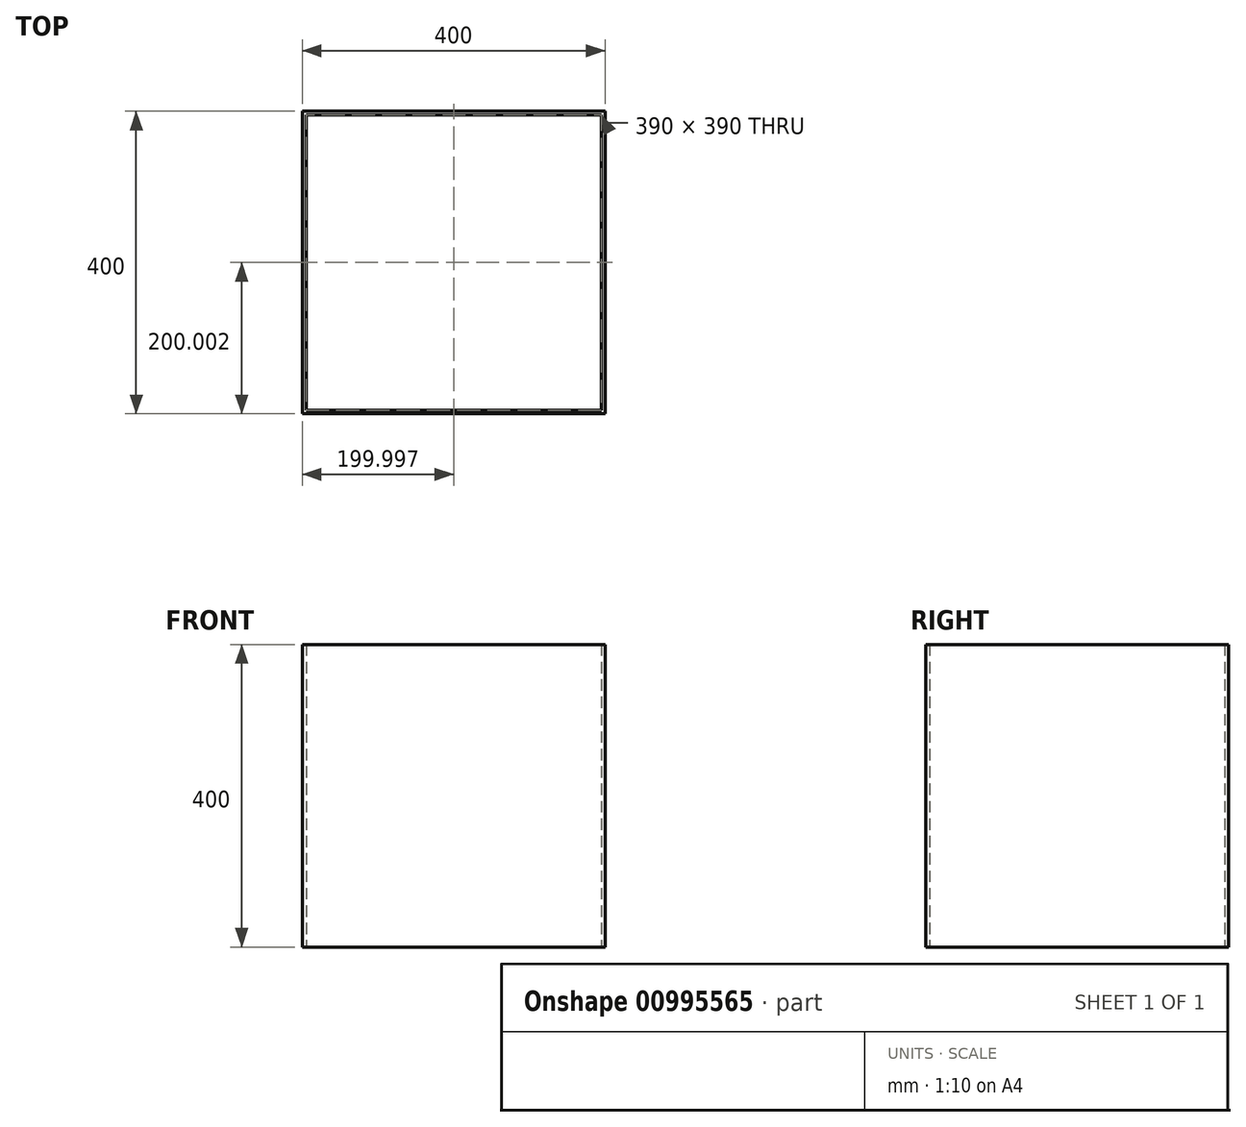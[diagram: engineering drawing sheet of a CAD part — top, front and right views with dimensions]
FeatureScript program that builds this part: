
annotation { "Feature Type Name" : "Feature", "Feature Type Description" : "" }
export const myFeature = defineFeature(function(context is Context, id is Id, definition is map)
    precondition{}
    {
        {
            var Q0;
            Q0=qCreatedBy(makeId("Top.planeOp"),FACE);
            var sketch = newSketch(context, id + "F0", { "sketchPlane" : qUnion([Q0])});
            skLineSegment(sketch, "E0.bottom", {"start": v(-73.44, -157.33) * mm, "end": v(-473.44, -157.33) * mm});
            skLineSegment(sketch, "E0.top", {"start": v(-73.44, 242.67) * mm, "end": v(-473.44, 242.67) * mm});
            skLineSegment(sketch, "E0.left", {"start": v(-73.44, -157.33) * mm, "end": v(-73.44, 242.67) * mm});
            skLineSegment(sketch, "E0.right", {"start": v(-473.44, -157.33) * mm, "end": v(-473.44, 242.67) * mm});
            skPoint(sketch, "E0.middle", {"position": v(-273.44, 42.67) * mm});
            skLineSegment(sketch, "E1.bottom", {"start": v(-78.44, 237.67) * mm, "end": v(-468.44, 237.67) * mm});
            skLineSegment(sketch, "E1.top", {"start": v(-78.44, -152.33) * mm, "end": v(-468.44, -152.33) * mm});
            skLineSegment(sketch, "E1.left", {"start": v(-78.44, 237.67) * mm, "end": v(-78.44, -152.33) * mm});
            skLineSegment(sketch, "E1.right", {"start": v(-468.44, 237.67) * mm, "end": v(-468.44, -152.33) * mm});
            skSolve(sketch);
        }
        {
            var Q0;
            Q0=makeQuery(id+"F0.imprint","IMPRINT",FACE,{"disambiguationData":[TD([[makeQuery(id+"F0.imprint","IMPRINT",EDGE,{"derivedFrom":sQuery(id+"F0.wireOp",EDGE,"E0.bottom")}),-1.0]])]});
            extrude(context, id + "F1", {"entities" : qUnion([Q0]), "depth" : 400 * mm, "offsetDistance" : 25 * mm});
        }
    });
